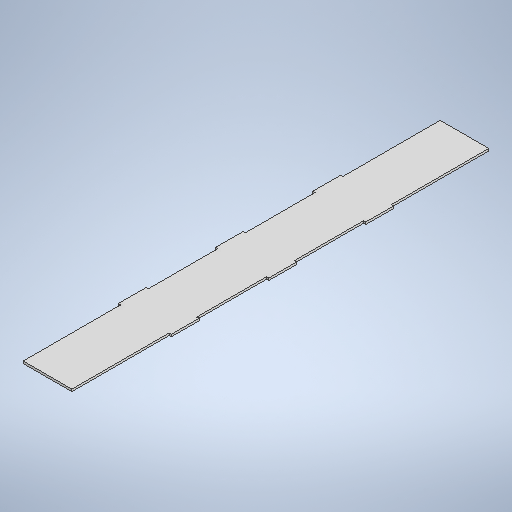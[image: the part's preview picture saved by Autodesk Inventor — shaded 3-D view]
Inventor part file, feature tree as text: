
AUTODESK INVENTOR PART (.ipt)
format: ipt  version: 2025.2 (Build 292293000, 293)  size: 267,776 bytes
history: native  units: mm
features: extrude x1, sketch x1
ambient origin geometry x8: Origin, YZ Plane, XZ Plane, XY Plane, X Axis, Y Axis, Z Axis, Center Point
bodies: Solid1 (feature_tree)
feature tree (2):
  extrude  "Extrusion1"  Depth=70.0mm
  sketch  "Sketch1"  dims[d0=600.0mm d2=70.0mm d3=600.0mm d7=40.0mm d8=100.0mm d9=40.0mm d10=100.0mm d11=40.0mm d12=3.175mm d13=0.0mm]
